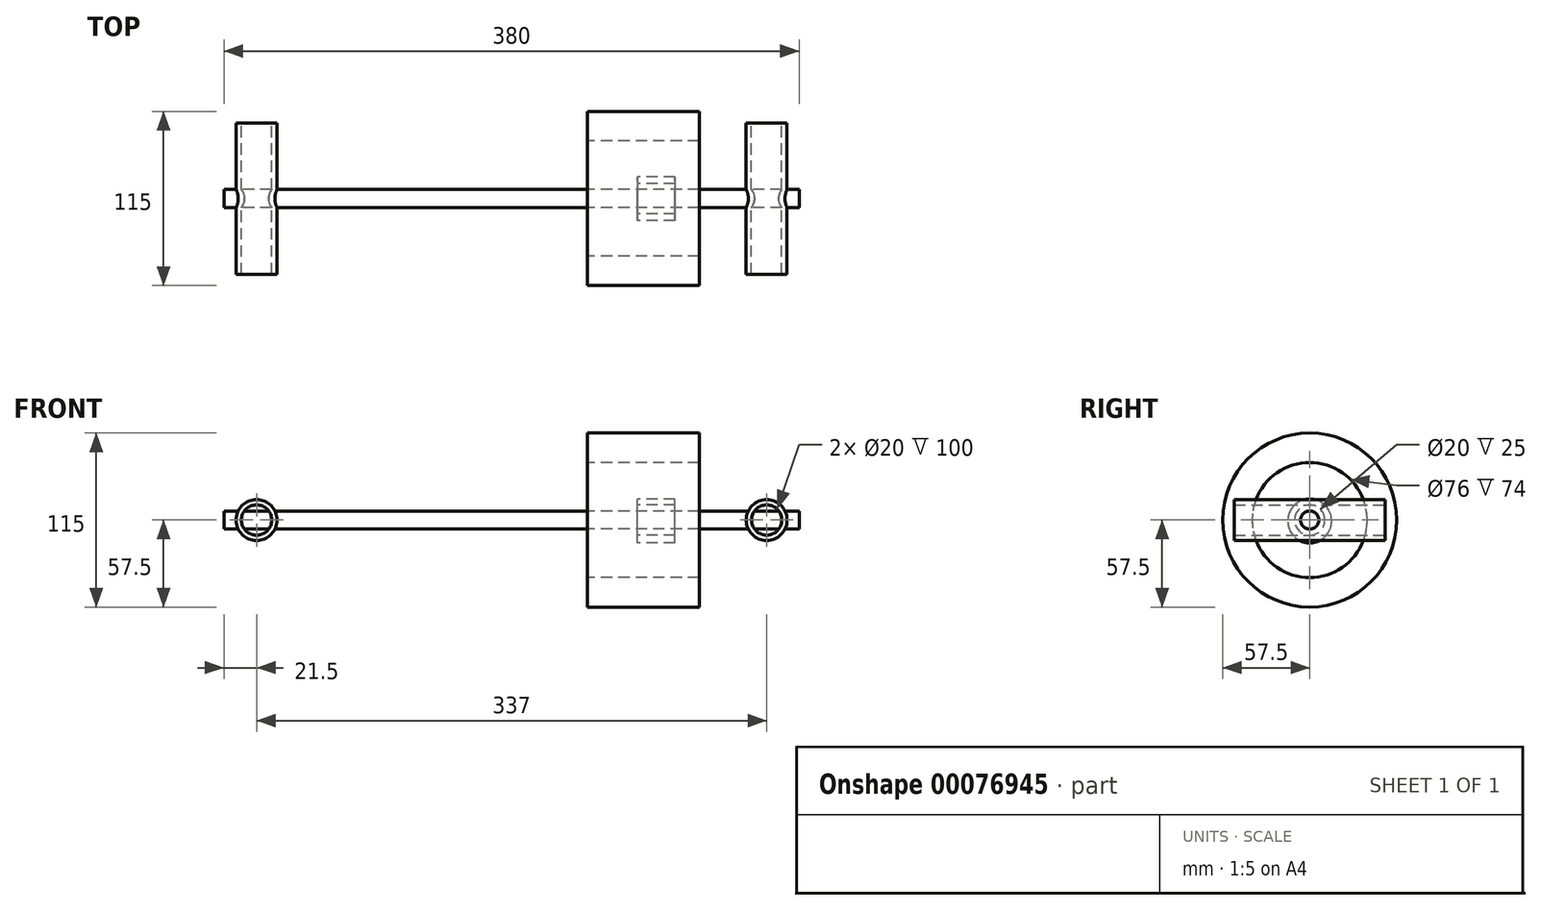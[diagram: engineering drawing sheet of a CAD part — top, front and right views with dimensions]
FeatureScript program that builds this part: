
annotation { "Feature Type Name" : "Feature", "Feature Type Description" : "" }
export const myFeature = defineFeature(function(context is Context, id is Id, definition is map)
    precondition{}
    {
        {
            var Q0;
            Q0=qCreatedBy(makeId("Right.planeOp"),FACE);
            var sketch = newSketch(context, id + "F0", { "sketchPlane" : qUnion([Q0])});
            skCircle(sketch, "E0", {"center": v(0, 0) * mm, "radius": 6 * mm});
            skSolve(sketch);
        }
        {
            var Q0;
            Q0 = qSketchRegion(id + "F0", true);
            extrude(context, id + "F1", {"entities" : qUnion([Q0]), "endBound" : BoundingType.SYMMETRIC, "depth" : 380 * mm});
        }
        {
            var Q0;
            Q0=qCreatedBy(makeId("Front.planeOp"),FACE);
            var sketch = newSketch(context, id + "F2", { "sketchPlane" : qUnion([Q0])});
            skCircle(sketch, "E1", {"center": v(168.5, 0) * mm, "radius": 13.5 * mm});
            skCircle(sketch, "E2", {"center": v(168.5, 0) * mm, "radius": 10 * mm});
            skCircle(sketch, "E3.MirrorC", {"center": v(-168.5, 0) * mm, "radius": 10 * mm});
            skCircle(sketch, "E4.MirrorC", {"center": v(-168.5, 0) * mm, "radius": 13.5 * mm});
            skSolve(sketch);
        }
        {
            var Q0;
            Q0 = qSketchRegion(id + "F2", true);
            extrude(context, id + "F3", {"entities" : qUnion([Q0]), "operationType" : NewBodyOperationType.ADD, "endBound" : BoundingType.SYMMETRIC, "depth" : 100 * mm});
        }
        {
            var Q0;
            Q0=qCreatedBy(makeId("Right.planeOp"),FACE);
            cPlane(context, id + "F4", {"entities" : qUnion([Q0]), "cplaneType" : CPlaneType.OFFSET, "offset" : 50 * mm, "width" : 150 * mm, "height" : 150 * mm});
        }
        {
            var Q0;
            Q0=qCreatedBy(id+"F4.planeOp",FACE);
            var sketch = newSketch(context, id + "F5", { "sketchPlane" : qUnion([Q0])});
            skCircle(sketch, "E5", {"center": v(0, 0) * mm, "radius": 57.5 * mm});
            skCircle(sketch, "E6", {"center": v(0, 0) * mm, "radius": 38 * mm});
            skSolve(sketch);
        }
        {
            var Q0;
            Q0=makeQuery(id+"F5.imprint","IMPRINT",FACE,{"disambiguationData":[TD([[makeQuery(id+"F5.imprint","IMPRINT",EDGE,{"derivedFrom":sQuery(id+"F5.wireOp",EDGE,"E5")}),1.0]])]});
            extrude(context, id + "F6", {"entities" : qUnion([Q0]), "depth" : 74 * mm});
        }
        {
            var Q0;
            Q0=qCreatedBy(id+"F4.planeOp",FACE);
            cPlane(context, id + "F7", {"entities" : qUnion([Q0]), "cplaneType" : CPlaneType.OFFSET, "offset" : 33 * mm, "width" : 150 * mm, "height" : 150 * mm});
        }
        {
            var Q0;
            Q0=qCreatedBy(id+"F7.planeOp",FACE);
            var sketch = newSketch(context, id + "F8", { "sketchPlane" : qUnion([Q0])});
            skCircle(sketch, "E7", {"center": v(0, 0) * mm, "radius": 10 * mm});
            skCircle(sketch, "E8", {"center": v(0, -0.65) * mm, "radius": 14.5 * mm});
            skSolve(sketch);
        }
        {
            var Q0;
            Q0 = qSketchRegion(id + "F8", true);
            extrude(context, id + "F9", {"entities" : qUnion([Q0]), "depth" : 25 * mm});
        }
    });
